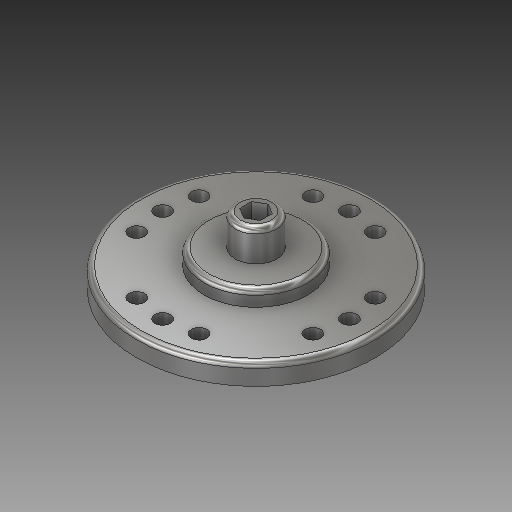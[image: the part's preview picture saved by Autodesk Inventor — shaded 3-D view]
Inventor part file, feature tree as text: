
AUTODESK INVENTOR PART (.ipt)
format: ipt  version: 2018 (Build 220112000, 112)  size: 230,912 bytes
history: imported  units: in
note: dims shown in document units (in); Inventor stores cm internally (conversion verified against a paired STEP export)
features: sketch x1, projected_geometry x1, other x1, imported_body x1
ambient origin geometry x8: Origin, YZ Plane, XZ Plane, XY Plane, X Axis, Y Axis, Z Axis, Center Point
bodies: Solid1 (imported_parasolid)
feature tree (4):
  sketch  "Sketch1"
  projected_geometry  "Projected Loop1"
  other  "Saliente-Extruir4"
  imported_body  NMx_Import_Brep_tag  [imported B-rep: ~33 faces, bbox_mm=[18.470563, 7.5, 20.735281]]
